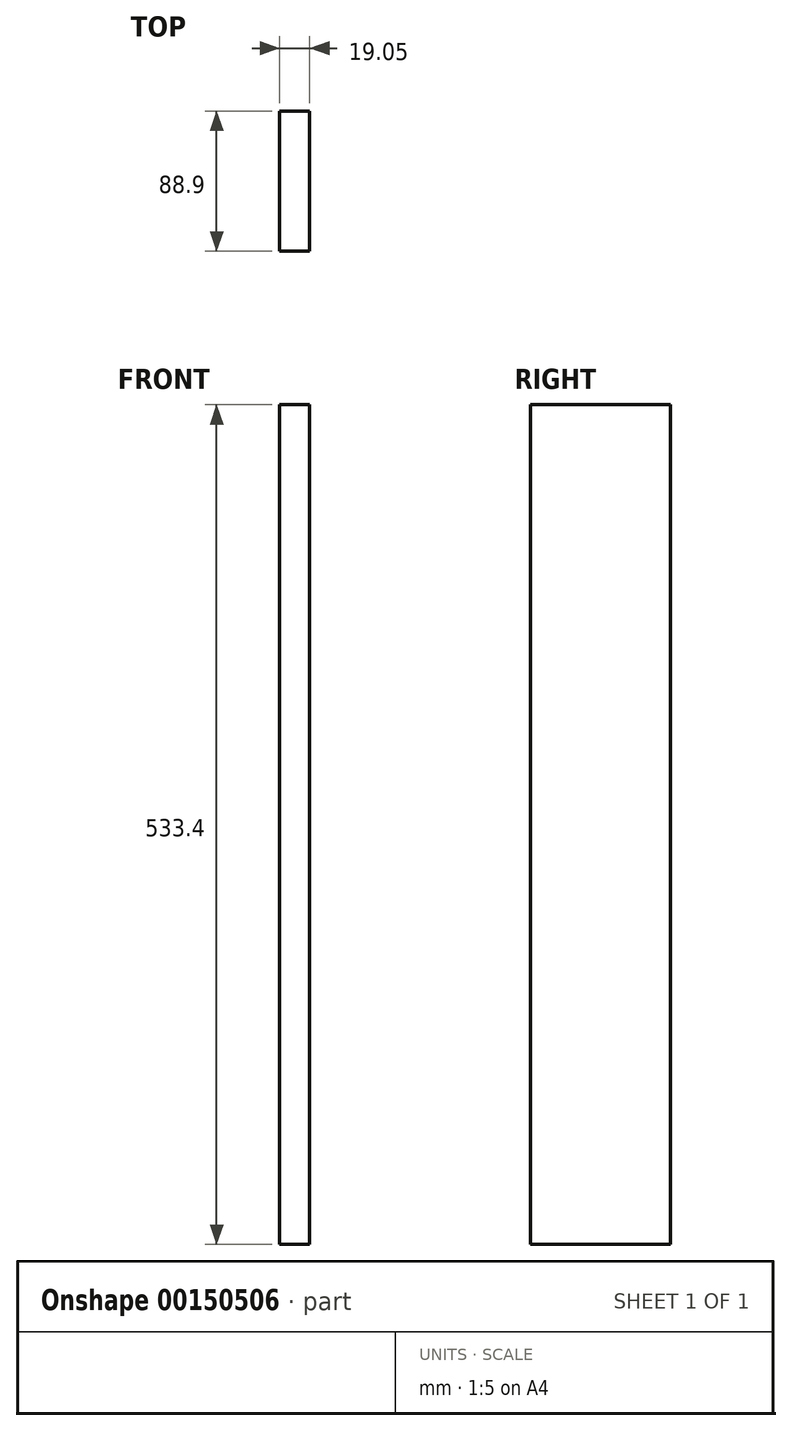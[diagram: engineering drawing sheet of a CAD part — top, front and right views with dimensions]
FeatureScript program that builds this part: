
annotation { "Feature Type Name" : "Feature", "Feature Type Description" : "" }
export const myFeature = defineFeature(function(context is Context, id is Id, definition is map)
    precondition{}
    {
        {
            var Q0;
            Q0=qCreatedBy(makeId("Right.planeOp"),FACE);
            var sketch = newSketch(context, id + "F0", { "sketchPlane" : qUnion([Q0])});
            skLineSegment(sketch, "E0.bottom", {"start": v(-53.15, 264.45) * mm, "end": v(35.75, 264.45) * mm});
            skLineSegment(sketch, "E0.top", {"start": v(-53.15, -268.95) * mm, "end": v(35.75, -268.95) * mm});
            skLineSegment(sketch, "E0.left", {"start": v(-53.15, 264.45) * mm, "end": v(-53.15, -268.95) * mm});
            skLineSegment(sketch, "E0.right", {"start": v(35.75, 264.45) * mm, "end": v(35.75, -268.95) * mm});
            skSolve(sketch);
        }
        {
            var Q0;
            Q0=makeQuery(id+"F0.imprint","IMPRINT",FACE,{"disambiguationData":[TD([[makeQuery(id+"F0.imprint","IMPRINT",EDGE,{"derivedFrom":sQuery(id+"F0.wireOp",EDGE,"E0.bottom")}),-1.0]])]});
            extrude(context, id + "F1", {"entities" : qUnion([Q0]), "depth" : 19.05 * mm});
        }
    });
